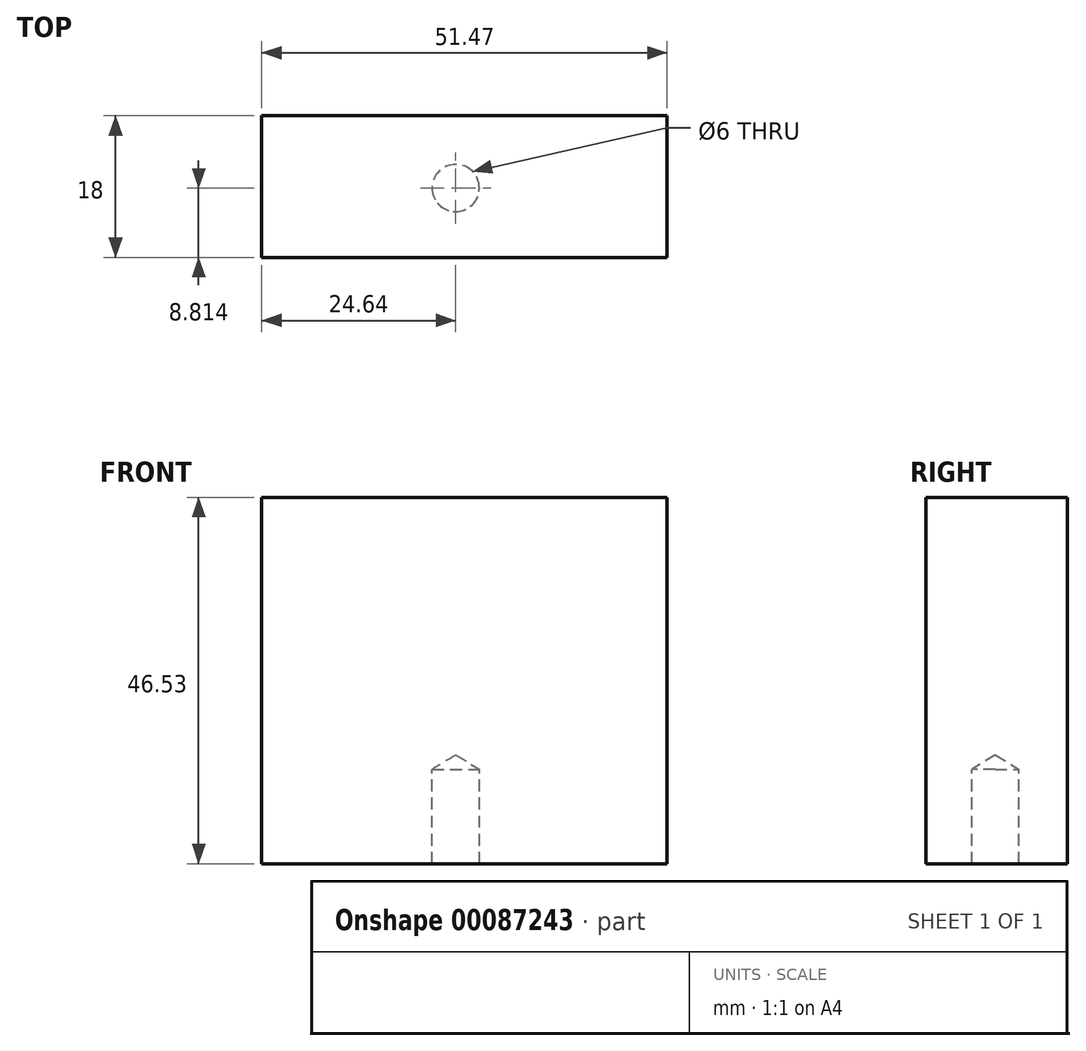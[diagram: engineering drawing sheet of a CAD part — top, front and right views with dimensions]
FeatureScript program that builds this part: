
annotation { "Feature Type Name" : "Feature", "Feature Type Description" : "" }
export const myFeature = defineFeature(function(context is Context, id is Id, definition is map)
    precondition{}
    {
        {
            var Q0;
            Q0=qCreatedBy(makeId("Front.planeOp"),FACE);
            var sketch = newSketch(context, id + "F0", { "sketchPlane" : qUnion([Q0])});
            skLineSegment(sketch, "E0.bottom", {"start": v(-22.4, 24.8) * mm, "end": v(29.08, 24.8) * mm});
            skLineSegment(sketch, "E0.top", {"start": v(-22.4, -21.74) * mm, "end": v(29.08, -21.74) * mm});
            skLineSegment(sketch, "E0.left", {"start": v(-22.4, 24.8) * mm, "end": v(-22.4, -21.74) * mm});
            skLineSegment(sketch, "E0.right", {"start": v(29.08, 24.8) * mm, "end": v(29.08, -21.74) * mm});
            skSolve(sketch);
        }
        {
            var Q0;
            Q0=makeQuery(id+"F0.imprint","IMPRINT",FACE,{"disambiguationData":[TD([[makeQuery(id+"F0.imprint","IMPRINT",EDGE,{"derivedFrom":sQuery(id+"F0.wireOp",EDGE,"E0.bottom")}),-1.0]])]});
            extrude(context, id + "F1", {"entities" : qUnion([Q0]), "depth" : 18 * mm});
        }
        {
            var Q0;
            Q0=makeQuery(id+"F1.opExtrude","SWEPT_FACE",FACE,{"disambiguationData":[OSD([sQuery(id+"F0.wireOp",EDGE,"E0.top")])]});
            var sketch = newSketch(context, id + "F2", { "sketchPlane" : qUnion([Q0])});
            skPoint(sketch, "E1", {"position": v(2.25, 9.19) * mm});
            skSolve(sketch);
        }
        {
            var Q0;
            Q0=sQuery(id+"F2.wireOp",VERTEX,"E1");
            var Q1;
            Q1=makeQuery(id+"F1.opExtrude","SWEPT_BODY",BODY,{"disambiguationData":[OSD([sQuery(id+"F0.wireOp",EDGE,"E0.bottom"),sQuery(id+"F0.wireOp",EDGE,"E0.top"),sQuery(id+"F0.wireOp",EDGE,"E0.left"),sQuery(id+"F0.wireOp",EDGE,"E0.right")])]});
            hole(context, id + "F3", {"style" : HoleStyle.SIMPLE, "endStyle" : HoleEndStyle.BLIND, "holeDiameter" : 6 * mm, "holeDepth" : 12 * mm, "startFromSketch" : true, "locations" : qUnion([Q0]), "scope" : qUnion([Q1])});
        }
    });
